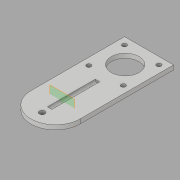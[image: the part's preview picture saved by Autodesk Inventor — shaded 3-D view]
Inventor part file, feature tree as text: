
AUTODESK INVENTOR PART (.ipt)
format: ipt  version: 2017 (Build 210142000, 142)  size: 108,544 bytes
history: native  units: mm
features: extrude x5, sketch x5, plane x1
ambient origin geometry x8: Origin, YZ Plane, XZ Plane, XY Plane, X Axis, Y Axis, Z Axis, Center Point
bodies: Solid1 (feature_tree)
feature tree (11):
  extrude  "Base"  Depth=4.0mm TaperAngle=0.0deg
  extrude  "Mounting Holes"  Depth=4.0mm
  extrude  "Pivot Hole"  Depth=25.0mm
  plane  "Work Plane2"
  extrude  "Support Ridge"  Depth=4.0mm
  extrude  "Shaft Hole"  [1 undecoded]
  sketch  "Sketch1"  dims[d0=4.0mm d1=0.0mm d9=4.0mm d10=0.0mm]
  sketch  "Sketch2"  dims[d11=4.0mm d12=0.0mm d14=4.0mm]
  sketch  "Sketch3"  dims[d15=31.75mm d16=11.25mm d17=0.0mm d18=0.0mm d19=25.0mm]
  sketch  "Sketch4"  dims[d20=4.0mm d21=0.0mm d22=44.0mm]
  sketch  "Sketch5"  dims[d24=5.0mm]
note: 1 required parameter value undecoded (feature->parameter linkage not recoverable at this tier; creation-order binding heuristic only, values carry confidence <= 0.55)
